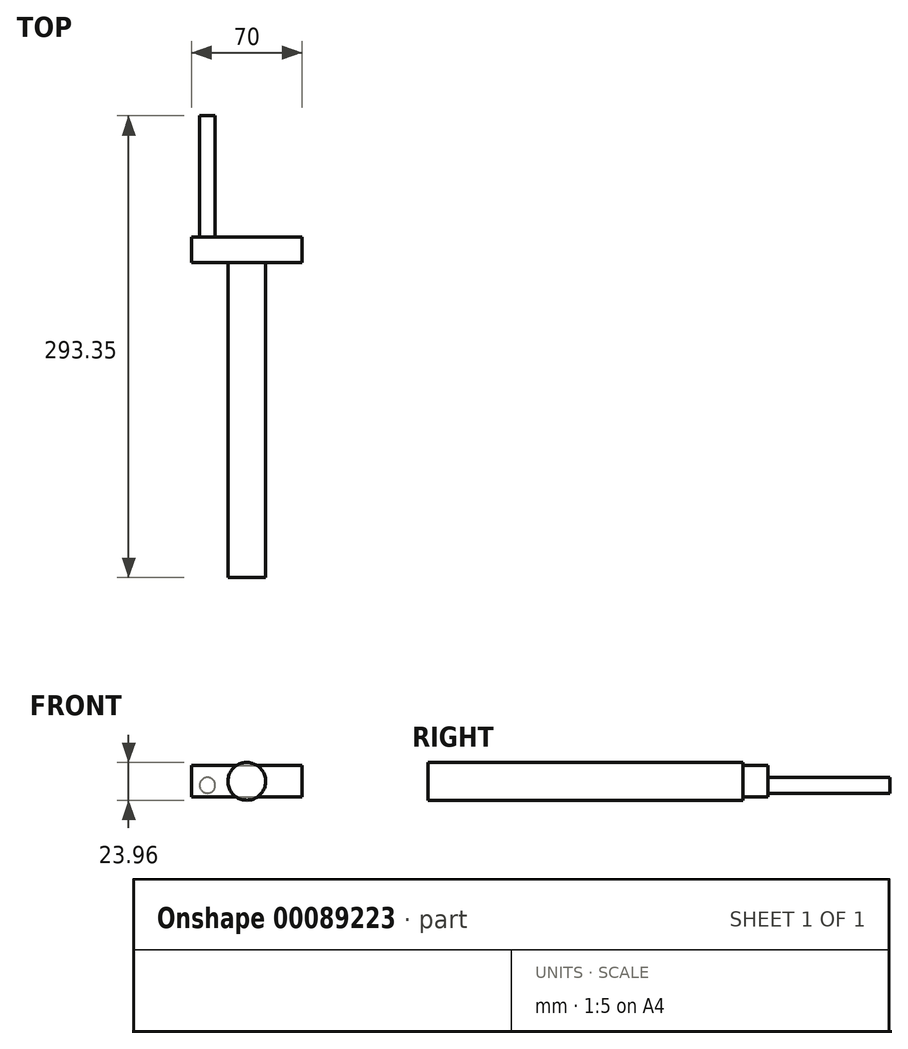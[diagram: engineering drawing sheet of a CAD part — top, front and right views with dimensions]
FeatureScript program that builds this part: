
annotation { "Feature Type Name" : "Feature", "Feature Type Description" : "" }
export const myFeature = defineFeature(function(context is Context, id is Id, definition is map)
    precondition{}
    {
        {
            var Q0;
            Q0=qCreatedBy(makeId("Front.planeOp"),FACE);
            cPlane(context, id + "F0", {"entities" : qUnion([Q0]), "cplaneType" : CPlaneType.OFFSET, "offset" : 50 * mm, "oppositeDirection" : true, "width" : 150 * mm, "height" : 150 * mm});
        }
        {
            var Q0;
            Q0=qCreatedBy(makeId("Front.planeOp"),FACE);
            var sketch = newSketch(context, id + "F1", { "sketchPlane" : qUnion([Q0])});
            skCircle(sketch, "E0", {"center": v(0, 0) * mm, "radius": 11.98 * mm});
            skSolve(sketch);
        }
        {
            var Q0;
            Q0=qCreatedBy(id+"F0.planeOp",FACE);
            var sketch = newSketch(context, id + "F2", { "sketchPlane" : qUnion([Q0])});
            skCircle(sketch, "E1", {"center": v(-25, -2.5) * mm, "radius": 5 * mm});
            skCircle(sketch, "E2.MirrorC", {"center": v(25, -2.5) * mm, "radius": 5 * mm});
            skSolve(sketch);
        }
        {
            var Q0;
            Q0 = qSketchRegion(id + "F1", true);
            extrude(context, id + "F3", {"entities" : qUnion([Q0]), "depth" : 200 * mm});
        }
        {
            var Q0;
            Q0=makeQuery(id+"F2.imprint","IMPRINT",FACE,{"disambiguationData":[TD([[makeQuery(id+"F2.imprint","IMPRINT",EDGE,{"derivedFrom":sQuery(id+"F2.wireOp",EDGE,"E1")}),1.0]])]});
            var Q1;
            Q1=makeQuery(id+"F2.imprint","IMPRINT",FACE,{"disambiguationData":[TD([[makeQuery(id+"F2.imprint","IMPRINT",EDGE,{"derivedFrom":sQuery(id+"F2.wireOp",EDGE,"E2.MirrorC")}),-1.0]])]});
            var Q2;
            Q2 = qConstructionFilter(qBodyType(qCreatedBy(id + "F2" ,EDGE), BodyType.WIRE), ConstructionObject.NO);
            extrude(context, id + "F4", {"entities" : qUnion([Q0, Q1]), "surfaceEntities" : qUnion([Q2]), "depth" : 48.85 * mm, "hasSecondDirection" : true, "secondDirectionOppositeDirection" : true, "secondDirectionDepth" : 43.35 * mm});
        }
        {
            var Q0;
            Q0=qCreatedBy(makeId("Top.planeOp"),FACE);
            var sketch = newSketch(context, id + "F5", { "sketchPlane" : qUnion([Q0])});
            skLineSegment(sketch, "E3.bottom", {"start": v(-35, 0) * mm, "end": v(35, 0) * mm});
            skLineSegment(sketch, "E3.top", {"start": v(-35, 16.15) * mm, "end": v(35, 16.15) * mm});
            skLineSegment(sketch, "E3.left", {"start": v(-35, 0) * mm, "end": v(-35, 16.15) * mm});
            skLineSegment(sketch, "E3.right", {"start": v(35, 0) * mm, "end": v(35, 16.15) * mm});
            skLineSegment(sketch, "E4.bottom", {"start": v(-35, 0) * mm, "end": v(-35, 0) * mm});
            skLineSegment(sketch, "E4.top", {"start": v(-35, 0) * mm, "end": v(-35, 0) * mm});
            skLineSegment(sketch, "E4.left", {"start": v(-35, 0) * mm, "end": v(-35, 0) * mm});
            skLineSegment(sketch, "E4.right", {"start": v(-35, 0) * mm, "end": v(-35, 0) * mm});
            skSolve(sketch);
        }
        {
            var Q0;
            Q0 = qSketchRegion(id + "F5", true);
            extrude(context, id + "F6", {"entities" : qUnion([Q0]), "operationType" : NewBodyOperationType.ADD, "depth" : 10 * mm, "hasSecondDirection" : true, "secondDirectionOppositeDirection" : true, "secondDirectionDepth" : 10 * mm});
        }
    });
